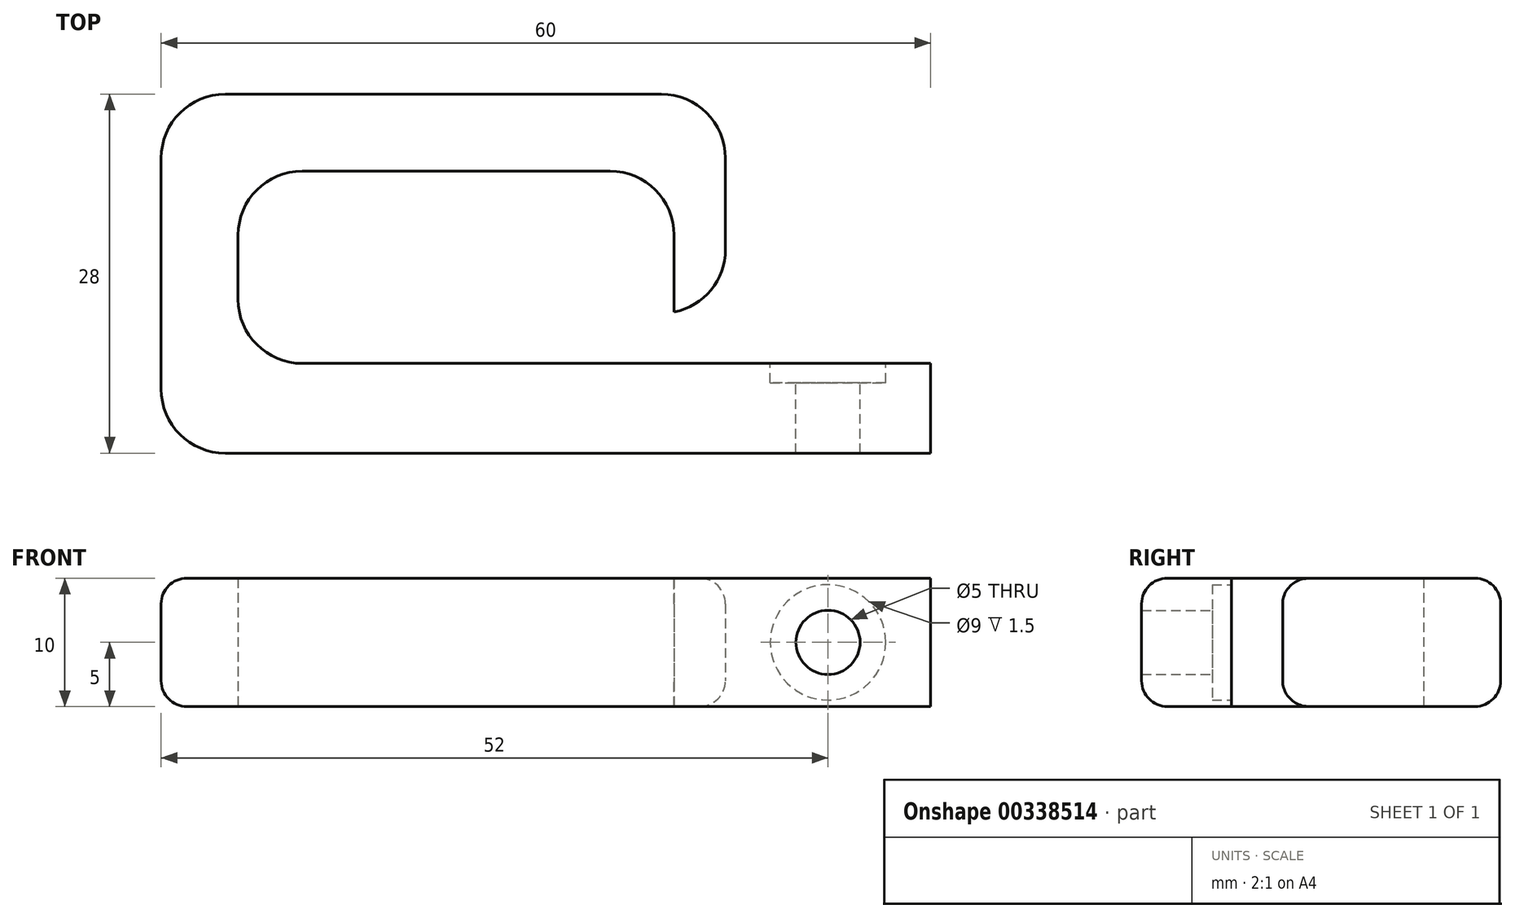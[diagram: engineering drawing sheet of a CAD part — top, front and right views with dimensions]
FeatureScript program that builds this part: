
annotation { "Feature Type Name" : "Feature", "Feature Type Description" : "" }
export const myFeature = defineFeature(function(context is Context, id is Id, definition is map)
    precondition{}
    {
        {
            var Q0;
            Q0=qCreatedBy(makeId("Top.planeOp"),FACE);
            var sketch = newSketch(context, id + "F0", { "sketchPlane" : qUnion([Q0])});
            skLineSegment(sketch, "E0", {"start": v(0, 0) * mm, "end": v(-60, 0) * mm});
            skLineSegment(sketch, "E1", {"start": v(-60, 0) * mm, "end": v(-60, 28) * mm});
            skLineSegment(sketch, "E2", {"start": v(-60, 28) * mm, "end": v(-16, 28) * mm});
            skLineSegment(sketch, "E3", {"start": v(-16, 28) * mm, "end": v(-16, 11) * mm});
            skLineSegment(sketch, "E4", {"start": v(-16, 11) * mm, "end": v(-20, 11) * mm});
            skLineSegment(sketch, "E5", {"start": v(-20, 11) * mm, "end": v(-20, 22) * mm});
            skLineSegment(sketch, "E6", {"start": v(-20, 22) * mm, "end": v(-54, 22) * mm});
            skLineSegment(sketch, "E7", {"start": v(-54, 22) * mm, "end": v(-54, 7) * mm});
            skLineSegment(sketch, "E8", {"start": v(-54, 7) * mm, "end": v(0, 7) * mm});
            skLineSegment(sketch, "E9", {"start": v(0, 7) * mm, "end": v(0, 0) * mm});
            skSolve(sketch);
        }
        {
            var Q0;
            Q0=makeQuery(id+"F0.imprint","IMPRINT",FACE,{"disambiguationData":[TD([[makeQuery(id+"F0.imprint","IMPRINT",EDGE,{"derivedFrom":sQuery(id+"F0.wireOp",EDGE,"E0")}),-1.0]])]});
            extrude(context, id + "F1", {"entities" : qUnion([Q0]), "offsetDistance" : 25 * mm, "depth" : 10 * mm});
        }
        {
            var Q0;
            Q0=makeQuery(id+"F1.opExtrude","SWEPT_FACE",FACE,{"disambiguationData":[OSD([sQuery(id+"F0.wireOp",EDGE,"E8")])]});
            var sketch = newSketch(context, id + "F2", { "sketchPlane" : qUnion([Q0])});
            skPoint(sketch, "E10", {"position": v(8, 5) * mm});
            skPoint(sketch, "E10.positionSnap0", {"position": v(0, 5) * mm});
            skPoint(sketch, "E11", {"position": v(22, 5) * mm});
            skSolve(sketch);
        }
        {
            var Q0;
            Q0=sQuery(id+"F2.wireOp",VERTEX,"E10");
            var Q1;
            Q1=makeQuery(id+"F1.opExtrude","SWEPT_BODY",BODY,{"disambiguationData":[OSD([sQuery(id+"F0.wireOp",EDGE,"E0"),sQuery(id+"F0.wireOp",EDGE,"E1"),sQuery(id+"F0.wireOp",EDGE,"E2"),sQuery(id+"F0.wireOp",EDGE,"E3"),sQuery(id+"F0.wireOp",EDGE,"E4"),sQuery(id+"F0.wireOp",EDGE,"E5"),sQuery(id+"F0.wireOp",EDGE,"E6"),sQuery(id+"F0.wireOp",EDGE,"E7"),sQuery(id+"F0.wireOp",EDGE,"E8"),sQuery(id+"F0.wireOp",EDGE,"E9")])]});
            hole(context, id + "F3", {"style" : HoleStyle.C_BORE, "endStyle" : HoleEndStyle.THROUGH, "holeDiameter" : 5 * mm, "cBoreDiameter" : 9 * mm, "cBoreDepth" : 1.5 * mm, "majorDiameter" : 5 * mm, "tappedDepth" : 12 * mm, "tapClearance" : 3, "locations" : qUnion([Q0]), "scope" : qUnion([Q1])});
        }
        {
            var Q0;
            Q0=makeQuery(id+"F1.opExtrude","SWEPT_EDGE",EDGE,{"disambiguationData":[OSD([sQuery(id+"F0.wireOp",EDGE,"E7"),sQuery(id+"F0.wireOp",EDGE,"E8")])]});
            var Q1;
            Q1=makeQuery(id+"F1.opExtrude","SWEPT_EDGE",EDGE,{"disambiguationData":[OSD([sQuery(id+"F0.wireOp",EDGE,"E5"),sQuery(id+"F0.wireOp",EDGE,"E6")])]});
            var Q2;
            Q2=makeQuery(id+"F1.opExtrude","SWEPT_EDGE",EDGE,{"disambiguationData":[OSD([sQuery(id+"F0.wireOp",EDGE,"E6"),sQuery(id+"F0.wireOp",EDGE,"E7")])]});
            var Q3;
            Q3=makeQuery(id+"F1.opExtrude","SWEPT_EDGE",EDGE,{"disambiguationData":[OSD([sQuery(id+"F0.wireOp",EDGE,"E0"),sQuery(id+"F0.wireOp",EDGE,"E1")])]});
            var Q4;
            Q4=makeQuery(id+"F1.opExtrude","SWEPT_EDGE",EDGE,{"disambiguationData":[OSD([sQuery(id+"F0.wireOp",EDGE,"E1"),sQuery(id+"F0.wireOp",EDGE,"E2")])]});
            var Q5;
            Q5=makeQuery(id+"F1.opExtrude","SWEPT_EDGE",EDGE,{"disambiguationData":[OSD([sQuery(id+"F0.wireOp",EDGE,"E2"),sQuery(id+"F0.wireOp",EDGE,"E3")])]});
            var Q6;
            Q6=makeQuery(id+"F1.opExtrude","SWEPT_EDGE",EDGE,{"disambiguationData":[OSD([sQuery(id+"F0.wireOp",EDGE,"E3"),sQuery(id+"F0.wireOp",EDGE,"E4")])]});
            fillet(context, id + "F4", {"entities" : qUnion([Q0, Q1, Q2, Q3, Q4, Q5, Q6]), "radius" : 5 * mm, "tangentPropagation" : true, "defaultsChanged" : false, "vertexSettings" : [], "allowEdgeOverflow" : false});
        }
        {
            var Q0;
            Q0=makeQuery(id+"F1.opExtrude","CAP_EDGE",EDGE,{"disambiguationData":[OSD([sQuery(id+"F0.wireOp",EDGE,"E2")])],"isStart":true});
            var Q1;
            Q1=makeQuery(id+"F1.opExtrude","SWEPT_FACE",FACE,{"disambiguationData":[OSD([sQuery(id+"F0.wireOp",EDGE,"E2")])]});
            var Q2;
            Q2=makeQuery(id+"F1.opExtrude","CAP_EDGE",EDGE,{"disambiguationData":[OSD([sQuery(id+"F0.wireOp",EDGE,"E3")])],"isStart":true});
            var Q3;
            Q3=makeQuery(id+"F1.opExtrude","CAP_EDGE",EDGE,{"disambiguationData":[OSD([sQuery(id+"F0.wireOp",EDGE,"E3")])],"isStart":false});
            var Q4;
            Q4=makeQuery(id+"F1.opExtrude","CAP_EDGE",EDGE,{"disambiguationData":[OSD([sQuery(id+"F0.wireOp",EDGE,"E1")])],"isStart":true});
            var Q5;
            Q5=makeQuery(id+"F1.opExtrude","CAP_EDGE",EDGE,{"disambiguationData":[OSD([sQuery(id+"F0.wireOp",EDGE,"E1")])],"isStart":false});
            fillet(context, id + "F5", {"entities" : qUnion([Q0, Q1, Q2, Q3, Q4, Q5]), "radius" : 2 * mm, "tangentPropagation" : true, "allowEdgeOverflow" : false});
        }
    });
